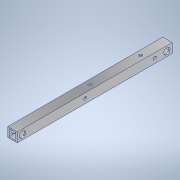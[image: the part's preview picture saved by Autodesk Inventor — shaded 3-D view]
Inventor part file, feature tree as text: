
AUTODESK INVENTOR PART (.ipt)
format: ipt  version: 2020.3 (Build 243373000, 373)  size: 181,760 bytes
history: native  units: mm
features: sketch x8, hole x5, extrude x3, other x1
ambient origin geometry x8: Origin, YZ Plane, XZ Plane, XY Plane, X Axis, Y Axis, Z Axis, Center Point
bodies: Body1 (feature_tree)
feature tree (17):
  other  "ソリッド1"
  extrude  "押し出し1"  Depth=9.0mm
  hole  "穴1"  [1 undecoded]
  hole  "穴2"  [1 undecoded]
  extrude  "押し出し3"  Depth=6.6mm
  hole  "穴4"  [1 undecoded]
  extrude  "押し出し4"  Depth=1.2mm
  hole  "穴5"  [1 undecoded]
  hole  "穴6"  [1 undecoded]
  sketch  "スケッチ1"
  sketch  "スケッチ2"
  sketch  "スケッチ3"
  sketch  "スケッチ6"
  sketch  "スケッチ7"
  sketch  "スケッチ8"
  sketch  "スケッチ9"
  sketch  "スケッチ10"
note: 5 required parameter values undecoded (feature->parameter linkage not recoverable at this tier; creation-order binding heuristic only, values carry confidence <= 0.55)
